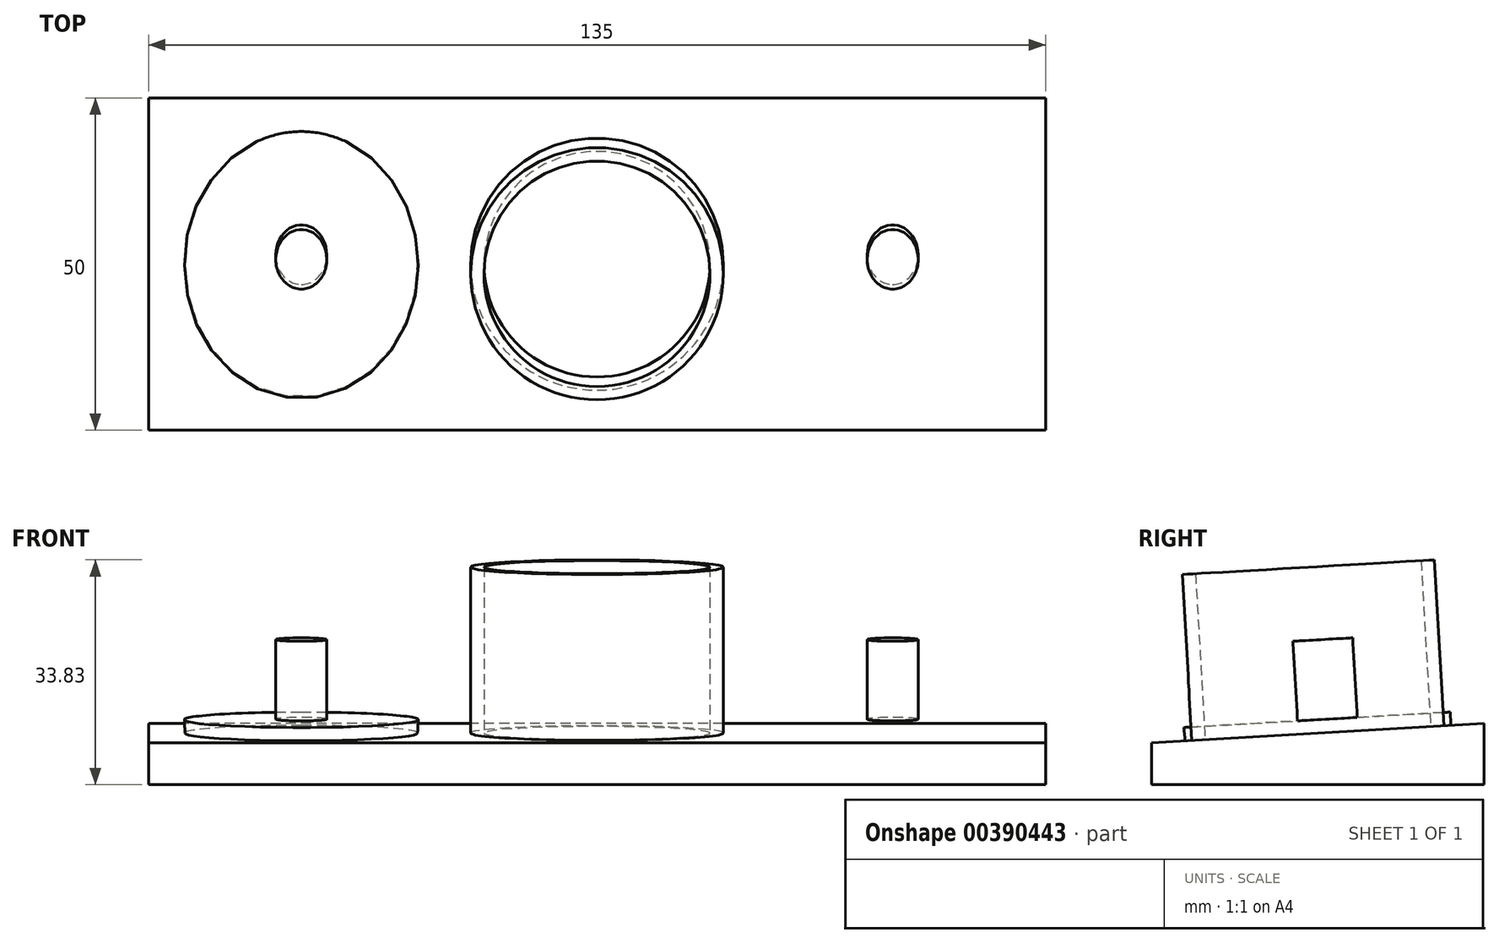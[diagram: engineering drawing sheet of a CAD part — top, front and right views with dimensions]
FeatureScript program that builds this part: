
annotation { "Feature Type Name" : "Feature", "Feature Type Description" : "" }
export const myFeature = defineFeature(function(context is Context, id is Id, definition is map)
    precondition{}
    {
        {
            var Q0;
            Q0=qCreatedBy(makeId("Right.planeOp"),FACE);
            var sketch = newSketch(context, id + "F0", { "sketchPlane" : qUnion([Q0])});
            skLineSegment(sketch, "E0", {"start": v(-72.72, 0) * mm, "end": v(-72.72, 6.32) * mm});
            skLineSegment(sketch, "E1", {"start": v(-72.72, 6.32) * mm, "end": v(-22.72, 9.22) * mm});
            skLineSegment(sketch, "E2", {"start": v(-22.72, 9.22) * mm, "end": v(-22.72, 0) * mm});
            skLineSegment(sketch, "E3", {"start": v(-22.72, 0) * mm, "end": v(-72.72, 0) * mm});
            skSolve(sketch);
        }
        {
            var Q0;
            Q0=makeQuery(id+"F0.imprint","IMPRINT",FACE,{"disambiguationData":[TD([[makeQuery(id+"F0.imprint","IMPRINT",EDGE,{"derivedFrom":sQuery(id+"F0.wireOp",EDGE,"E0")}),-1.0]])]});
            extrude(context, id + "F1", {"entities" : qUnion([Q0]), "depth" : 135 * mm});
        }
        {
            var Q0;
            Q0=makeQuery(id+"F1.opExtrude","SWEPT_FACE",FACE,{"disambiguationData":[OSD([sQuery(id+"F0.wireOp",EDGE,"E1")])]});
            var sketch = newSketch(context, id + "F2", { "sketchPlane" : qUnion([Q0])});
            skLineSegment(sketch, "E4", {"start": v(0, -47.2) * mm, "end": v(135, -47.2) * mm, "construction": true});
            skLineSegment(sketch, "E5", {"start": v(67.5, -22.15) * mm, "end": v(67.5, -72.24) * mm, "construction": true});
            skEllipse(sketch, "E6", {"center": v(23, -47.2) * mm, "majorRadius": 20 * mm, "minorRadius": 17.5 * mm, "majorAxis": v(0, -1)});
            skEllipse(sketch, "E7.MirrorC", {"center": v(112, -47.2) * mm, "majorRadius": 20 * mm, "minorRadius": 17.5 * mm, "majorAxis": v(0, -1)});
            skEllipse(sketch, "E8.MirrorC", {"center": v(112, -47.2) * mm, "majorRadius": 20 * mm, "minorRadius": 17.5 * mm, "majorAxis": v(0, -1)});
            skEllipse(sketch, "E9.MirrorC", {"center": v(112, -47.2) * mm, "majorRadius": 20 * mm, "minorRadius": 17.5 * mm, "majorAxis": v(0, -1)});
            skEllipse(sketch, "E10.MirrorC", {"center": v(112, -47.2) * mm, "majorRadius": 20 * mm, "minorRadius": 17.5 * mm, "majorAxis": v(0, -1)});
            skSolve(sketch);
        }
        {
            var Q0;
            Q0 = qSketchRegion(id + "F4", true);
            var Q1;
            Q1=makeQuery(id+"F2.imprint","IMPRINT",FACE,{"disambiguationData":[TD([[makeQuery(id+"F2.imprint","IMPRINT",EDGE,{"derivedFrom":sQuery(id+"F2.wireOp",EDGE,"E6")}),1.0]])]});
            var Q2;
            Q2=makeQuery(id+"F2.imprint","IMPRINT",FACE,{"disambiguationData":[TD([[makeQuery(id+"F2.imprint","IMPRINT",EDGE,{"derivedFrom":sQuery(id+"F2.wireOp",EDGE,"E10.MirrorC")}),1.0]])]});
            extrude(context, id + "F3", {"entities" : qUnion([Q0, Q1, Q2]), "operationType" : NewBodyOperationType.ADD, "depth" : 2 * mm, "hasDraft" : true, "draftAngle" : 3 * degree});
        }
        {
            var Q0;
            Q0=makeQuery(id+"F3.opExtrude","CAP_FACE",FACE,{"disambiguationData":[OSD([sQuery(id+"F2.wireOp",EDGE,"E6")])],"isStart":false});
            var sketch = newSketch(context, id + "F4", { "sketchPlane" : qUnion([Q0])});
            skEllipse(sketch, "E11", {"center": v(23, -45.64) * mm, "majorRadius": 4.5 * mm, "minorRadius": 3.85 * mm, "majorAxis": v(0, -1)});
            skEllipse(sketch, "E12.MirrorC", {"center": v(112, -45.64) * mm, "majorRadius": 4.5 * mm, "minorRadius": 3.85 * mm, "majorAxis": v(0, -1)});
            skSolve(sketch);
        }
        {
            var Q0;
            Q0=makeQuery(id+"F4.imprint","IMPRINT",FACE,{"disambiguationData":[TD([[makeQuery(id+"F4.imprint","IMPRINT",EDGE,{"derivedFrom":sQuery(id+"F4.wireOp",EDGE,"E11")}),1.0]])]});
            var Q1;
            Q1=makeQuery(id+"F4.imprint","IMPRINT",FACE,{"disambiguationData":[TD([[makeQuery(id+"F4.imprint","IMPRINT",EDGE,{"derivedFrom":sQuery(id+"F4.wireOp",EDGE,"E12.MirrorC")}),1.0]])]});
            var Q2;
            Q2=sQuery(id+"F4.wireOp",EDGE,"E11");
            var Q3;
            Q3=sQuery(id+"F4.wireOp",EDGE,"E12.MirrorC");
            extrude(context, id + "F5", {"entities" : qUnion([Q0, Q1]), "operationType" : NewBodyOperationType.ADD, "surfaceEntities" : qUnion([Q2, Q3]), "depth" : 12 * mm});
        }
        {
            var Q0;
            Q0=makeQuery(id+"F2.imprint","IMPRINT",FACE,{"disambiguationData":[TD([[makeQuery(id+"F2.imprint","IMPRINT",EDGE,{"derivedFrom":sQuery(id+"F2.wireOp",EDGE,"E6")}),-1.0]])]});
            var sketch = newSketch(context, id + "F6", { "sketchPlane" : qUnion([Q0])});
            skCircle(sketch, "E13", {"center": v(67.5, -47.2) * mm, "radius": 17 * mm});
            skCircle(sketch, "E14.0", {"center": v(67.5, -47.2) * mm, "radius": 19 * mm});
            skSolve(sketch);
        }
        {
            var Q0;
            Q0=makeQuery(id+"F6.imprint","IMPRINT",FACE,{"disambiguationData":[TD([[makeQuery(id+"F6.imprint","IMPRINT",EDGE,{"derivedFrom":sQuery(id+"F6.wireOp",EDGE,"E13")}),-1.0]])]});
            var Q1;
            Q1=sQuery(id+"F6.wireOp",EDGE,"E13");
            var Q2;
            Q2=sQuery(id+"F6.wireOp",EDGE,"E14.0");
            extrude(context, id + "F7", {"entities" : qUnion([Q0]), "operationType" : NewBodyOperationType.ADD, "surfaceEntities" : qUnion([Q1, Q2]), "depth" : 25 * mm});
        }
    });
